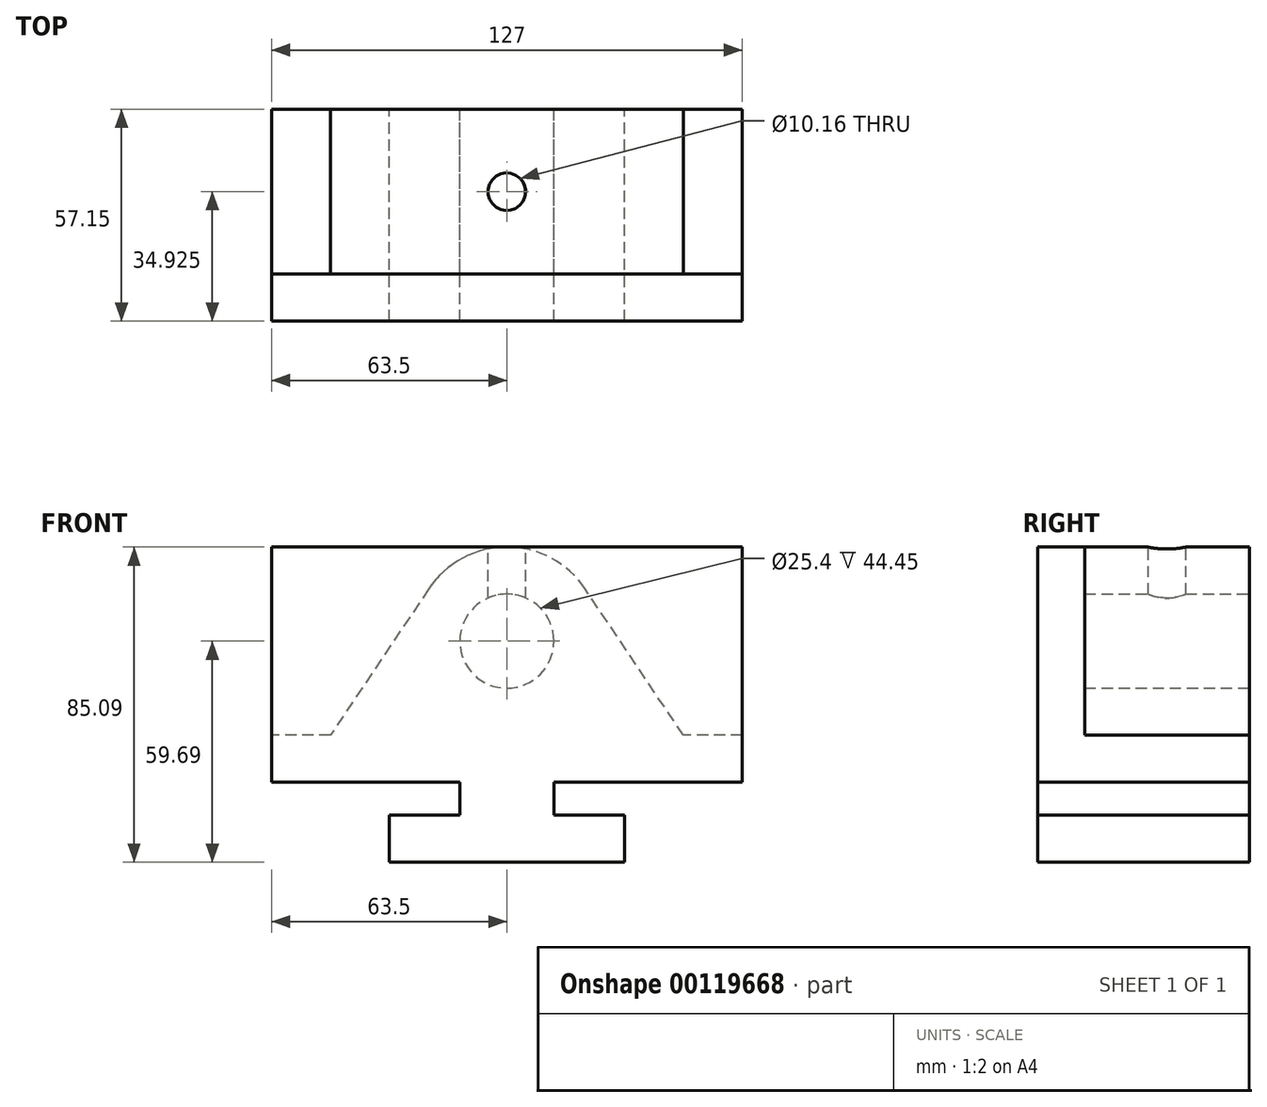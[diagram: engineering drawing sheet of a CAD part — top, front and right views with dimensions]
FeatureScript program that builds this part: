
annotation { "Feature Type Name" : "Feature", "Feature Type Description" : "" }
export const myFeature = defineFeature(function(context is Context, id is Id, definition is map)
    precondition{}
    {
        {
            var Q0;
            Q0=qCreatedBy(makeId("Front.planeOp"),FACE);
            var sketch = newSketch(context, id + "F0", { "sketchPlane" : qUnion([Q0])});
            skLineSegment(sketch, "E0", {"start": v(0, 0) * mm, "end": v(31.75, 0) * mm});
            skLineSegment(sketch, "E1", {"start": v(31.75, 0) * mm, "end": v(31.75, 12.7) * mm});
            skLineSegment(sketch, "E2", {"start": v(31.75, 12.7) * mm, "end": v(12.7, 12.7) * mm});
            skLineSegment(sketch, "E3", {"start": v(12.7, 12.7) * mm, "end": v(12.7, 21.59) * mm});
            skLineSegment(sketch, "E4", {"start": v(12.7, 21.59) * mm, "end": v(63.5, 21.6) * mm});
            skLineSegment(sketch, "E5", {"start": v(63.5, 21.59) * mm, "end": v(63.5, 34.3) * mm});
            skLineSegment(sketch, "E6", {"start": v(63.5, 34.3) * mm, "end": v(47.62, 34.3) * mm});
            skLineSegment(sketch, "E7", {"start": v(47.62, 34.29) * mm, "end": v(21.1, 73.84) * mm});
            skArc(sketch, "E8", {"start": v(21.1, 73.84) * mm, "mid": v(0, 85.1) * mm, "end": v(-21.1, 73.84) * mm});
            skLineSegment(sketch, "E9", {"start": v(-21.1, 73.84) * mm, "end": v(-47.62, 34.29) * mm});
            skLineSegment(sketch, "E10", {"start": v(-47.62, 34.3) * mm, "end": v(-63.5, 34.3) * mm});
            skLineSegment(sketch, "E11", {"start": v(-63.5, 34.3) * mm, "end": v(-63.5, 21.59) * mm});
            skLineSegment(sketch, "E12", {"start": v(-63.5, 21.59) * mm, "end": v(-12.7, 21.59) * mm});
            skLineSegment(sketch, "E13", {"start": v(-12.7, 21.59) * mm, "end": v(-12.7, 12.7) * mm});
            skLineSegment(sketch, "E14", {"start": v(-31.75, 12.7) * mm, "end": v(-12.7, 12.7) * mm});
            skLineSegment(sketch, "E15", {"start": v(-31.75, 0) * mm, "end": v(-31.75, 12.7) * mm});
            skLineSegment(sketch, "E16", {"start": v(0, 0) * mm, "end": v(-31.75, 0) * mm});
            skPoint(sketch, "E17.startSnap0", {"position": v(0, 85.1) * mm});
            skCircle(sketch, "E18", {"center": v(0, 59.7) * mm, "radius": 12.7 * mm});
            skPoint(sketch, "E19.orphan", {"position": v(-63.5, 85.1) * mm});
            skPoint(sketch, "E20.start.orphan", {"position": v(63.5, 85.09) * mm});
            skSolve(sketch);
        }
        {
            var Q0;
            Q0=makeQuery(id+"F0.imprint","IMPRINT",FACE,{"disambiguationData":[TD([[makeQuery(id+"F0.imprint","IMPRINT",EDGE,{"derivedFrom":sQuery(id+"F0.wireOp",EDGE,"E0")}),1.0]])]});
            var Q1;
            Q1=makeQuery(id+"F0.imprint","IMPRINT",FACE,{"disambiguationData":[TD([[makeQuery(id+"F0.imprint","IMPRINT",EDGE,{"derivedFrom":sQuery(id+"F0.wireOp",EDGE,"E18")}),1.0]])]});
            extrude(context, id + "F1", {"entities" : qUnion([Q0, Q1]), "depth" : 57.15 * mm});
        }
        {
            var Q0;
            Q0=makeQuery(id+"F1.opExtrude","CAP_FACE",FACE,{"disambiguationData":[OSD([sQuery(id+"F0.wireOp",EDGE,"E0"),sQuery(id+"F0.wireOp",EDGE,"E1"),sQuery(id+"F0.wireOp",EDGE,"E2"),sQuery(id+"F0.wireOp",EDGE,"E3"),sQuery(id+"F0.wireOp",EDGE,"E4"),sQuery(id+"F0.wireOp",EDGE,"E5"),sQuery(id+"F0.wireOp",EDGE,"E6"),sQuery(id+"F0.wireOp",EDGE,"E7"),sQuery(id+"F0.wireOp",EDGE,"E8"),sQuery(id+"F0.wireOp",EDGE,"E9"),sQuery(id+"F0.wireOp",EDGE,"E10"),sQuery(id+"F0.wireOp",EDGE,"E11"),sQuery(id+"F0.wireOp",EDGE,"E12"),sQuery(id+"F0.wireOp",EDGE,"E13"),sQuery(id+"F0.wireOp",EDGE,"E14"),sQuery(id+"F0.wireOp",EDGE,"E15"),sQuery(id+"F0.wireOp",EDGE,"E16")])],"isStart":false});
            var sketch = newSketch(context, id + "F2", { "sketchPlane" : qUnion([Q0])});
            skLineSegment(sketch, "E21.bottom", {"start": v(-63.5, 21.59) * mm, "end": v(63.5, 21.59) * mm});
            skLineSegment(sketch, "E21.top", {"start": v(-63.5, 85.09) * mm, "end": v(63.5, 85.09) * mm});
            skLineSegment(sketch, "E21.left", {"start": v(-63.5, 21.59) * mm, "end": v(-63.5, 85.09) * mm});
            skLineSegment(sketch, "E21.right", {"start": v(63.5, 21.59) * mm, "end": v(63.5, 85.09) * mm});
            skSolve(sketch);
        }
        {
            var Q0;
            Q0 = qSketchRegion(id + "F2", true);
            extrude(context, id + "F3", {"entities" : qUnion([Q0]), "operationType" : NewBodyOperationType.ADD, "oppositeDirection" : true, "depth" : 12.7 * mm});
        }
        {
            var Q0;
            Q0=makeQuery(id+"F0.imprint","IMPRINT",FACE,{"disambiguationData":[TD([[makeQuery(id+"F0.imprint","IMPRINT",EDGE,{"derivedFrom":sQuery(id+"F0.wireOp",EDGE,"E18")}),1.0]])]});
            var Q1;
            Q1=sQuery(id+"F0.wireOp",EDGE,"E18");
            extrude(context, id + "F4", {"entities" : qUnion([Q0]), "operationType" : NewBodyOperationType.REMOVE, "surfaceEntities" : qUnion([Q1]), "depth" : 44.45 * mm});
        }
        {
            var Q0;
            Q0=makeQuery(id+"F3.opExtrude","SWEPT_FACE",FACE,{"disambiguationData":[OSD([sQuery(id+"F2.wireOp",EDGE,"E21.top")])]});
            var sketch = newSketch(context, id + "F5", { "sketchPlane" : qUnion([Q0])});
            skLineSegment(sketch, "E22", {"start": v(0, 0) * mm, "end": v(0, -57.15) * mm, "construction": true});
            skCircle(sketch, "E23", {"center": v(0, -22.23) * mm, "radius": 5.08 * mm});
            skSolve(sketch);
        }
        {
            var Q0;
            Q0=makeQuery(id+"F5.imprint","IMPRINT",FACE,{"disambiguationData":[TD([[makeQuery(id+"F5.imprint","IMPRINT",EDGE,{"derivedFrom":sQuery(id+"F5.wireOp",EDGE,"E23")}),1.0]])]});
            extrude(context, id + "F6", {"entities" : qUnion([Q0]), "operationType" : NewBodyOperationType.REMOVE, "endBound" : BoundingType.UP_TO_NEXT, "oppositeDirection" : true, "depth" : 25.4 * mm});
        }
    });
